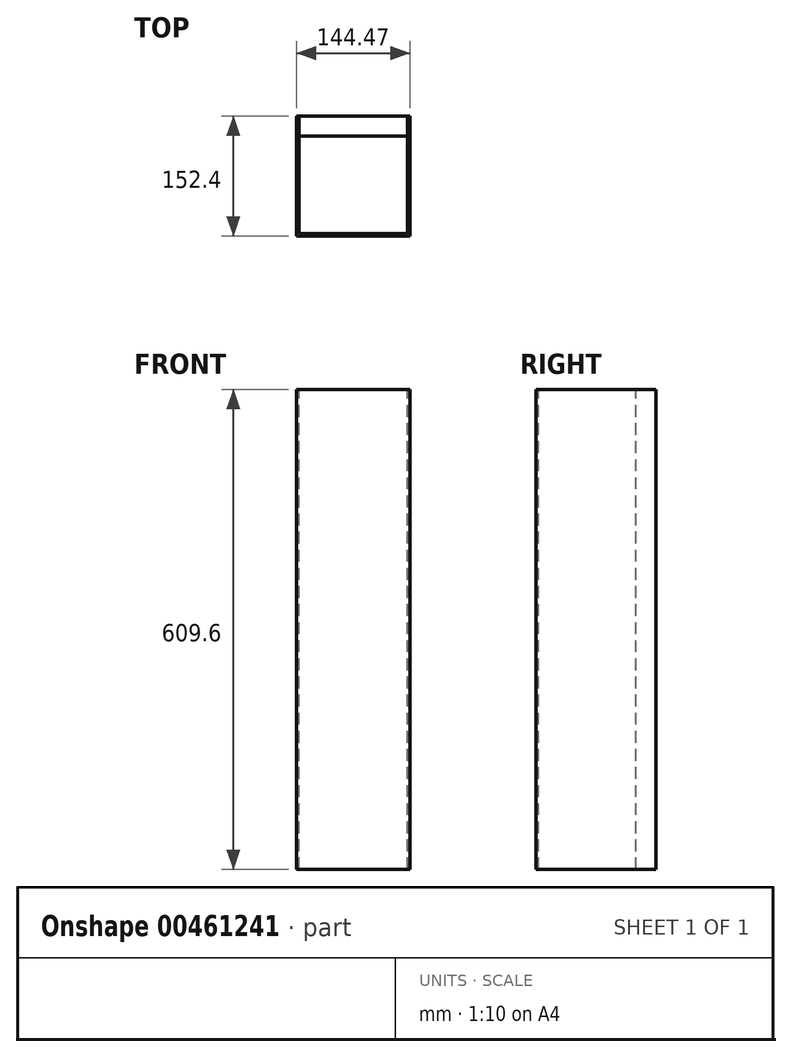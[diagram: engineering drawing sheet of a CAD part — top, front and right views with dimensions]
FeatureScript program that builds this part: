
annotation { "Feature Type Name" : "Feature", "Feature Type Description" : "" }
export const myFeature = defineFeature(function(context is Context, id is Id, definition is map)
    precondition{}
    {
        {
            var Q0;
            Q0=qCreatedBy(makeId("Front.planeOp"),FACE);
            var sketch = newSketch(context, id + "F0", { "sketchPlane" : qUnion([Q0])});
            skLineSegment(sketch, "E0.bottom", {"start": v(0, 0) * mm, "end": v(138.13, 0) * mm});
            skLineSegment(sketch, "E0.top", {"start": v(0, 609.6) * mm, "end": v(138.13, 609.6) * mm});
            skLineSegment(sketch, "E0.left", {"start": v(0, 0) * mm, "end": v(0, 609.6) * mm});
            skLineSegment(sketch, "E0.right", {"start": v(138.13, 0) * mm, "end": v(138.13, 609.6) * mm});
            skSolve(sketch);
        }
        {
            var Q0;
            Q0 = qSketchRegion(id + "F0", true);
            extrude(context, id + "F1", {"entities" : qUnion([Q0]), "depth" : 25.4 * mm});
        }
        {
            var Q0;
            Q0=makeQuery(id+"F1.opExtrude","SWEPT_FACE",FACE,{"disambiguationData":[OSD([sQuery(id+"F0.wireOp",EDGE,"E0.top")])]});
            var sketch = newSketch(context, id + "F2", { "sketchPlane" : qUnion([Q0])});
            skLineSegment(sketch, "E1", {"start": v(0, 0) * mm, "end": v(-3.17, 0) * mm});
            skLineSegment(sketch, "E2", {"start": v(-3.17, 0) * mm, "end": v(-3.17, -152.4) * mm});
            skLineSegment(sketch, "E3", {"start": v(-3.17, -152.4) * mm, "end": v(141.3, -152.4) * mm});
            skLineSegment(sketch, "E4", {"start": v(141.3, -152.4) * mm, "end": v(141.3, 0) * mm});
            skLineSegment(sketch, "E5", {"start": v(141.3, 0) * mm, "end": v(138.13, 0) * mm});
            skLineSegment(sketch, "E6", {"start": v(138.13, 0) * mm, "end": v(138.13, -149.22) * mm});
            skLineSegment(sketch, "E7", {"start": v(138.13, -149.22) * mm, "end": v(0, -149.22) * mm});
            skLineSegment(sketch, "E8", {"start": v(0, -149.22) * mm, "end": v(0, 0) * mm});
            skSolve(sketch);
        }
        {
            var Q0;
            Q0 = qSketchRegion(id + "F2", true);
            extrude(context, id + "F3", {"entities" : qUnion([Q0]), "oppositeDirection" : true, "depth" : 609.6 * mm});
        }
    });
